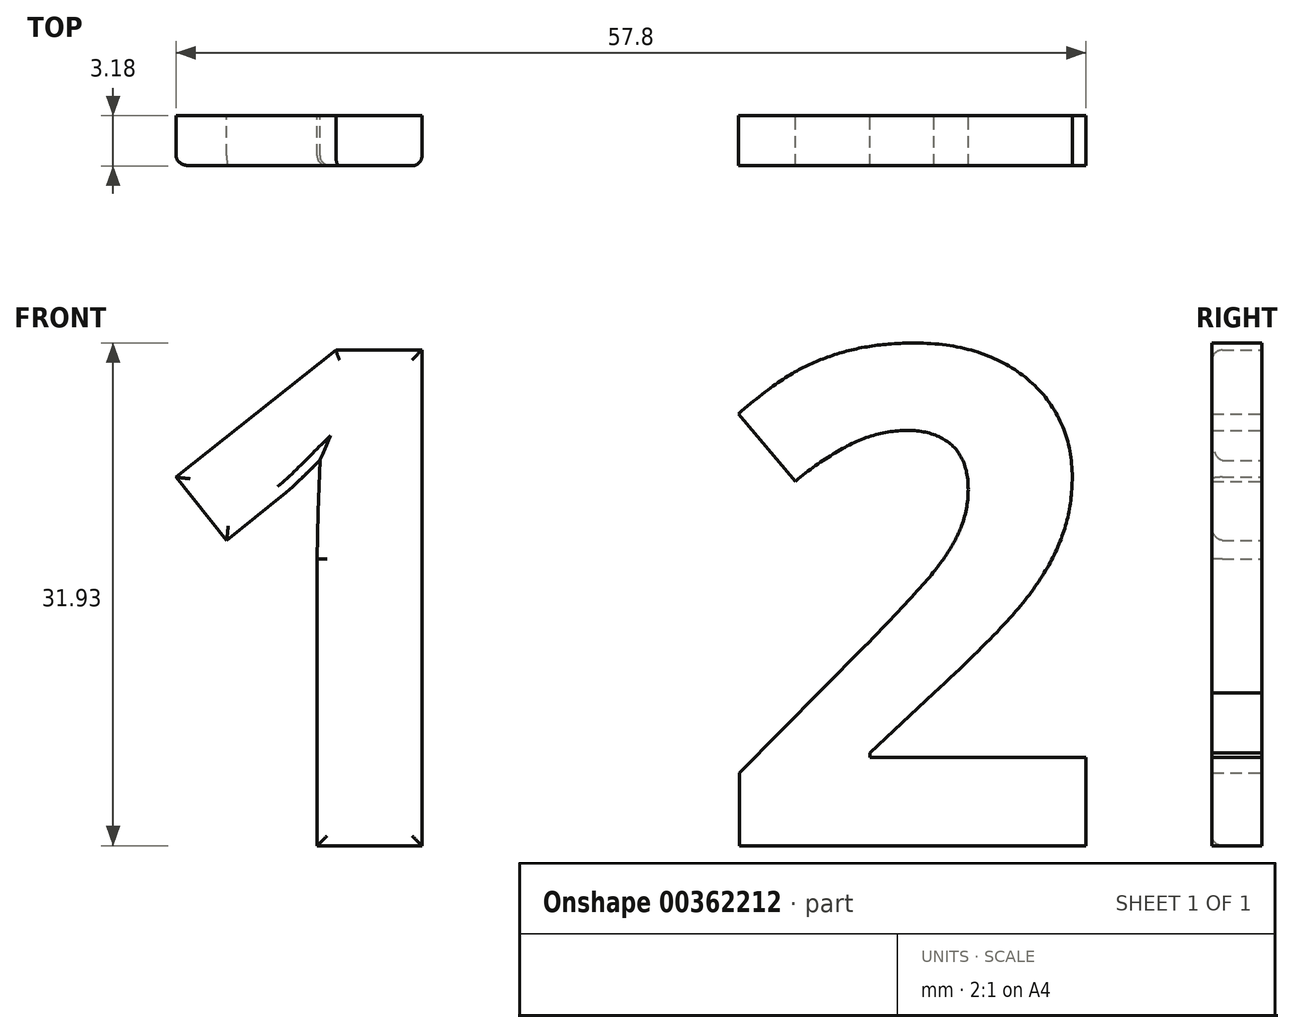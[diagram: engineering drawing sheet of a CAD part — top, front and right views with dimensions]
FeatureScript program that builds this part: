
annotation { "Feature Type Name" : "Feature", "Feature Type Description" : "" }
export const myFeature = defineFeature(function(context is Context, id is Id, definition is map)
    precondition{}
    {
        {
            var Q0;
            Q0=qCreatedBy(makeId("Front.planeOp"),FACE);
            var sketch = newSketch(context, id + "F0", { "sketchPlane" : qUnion([Q0])});
            skText(sketch, "E0", { "text": "1 2", "fontName": "OpenSans-Bold.ttf"});
            const initialGuessF0  = {"E0": [0, -0.03175, 1, 0, 0.03175]};
            skSetInitialGuess(sketch, initialGuessF0);
            skSolve(sketch);
        }
        {
            var Q0;
            Q0 = qSketchRegion(id + "F0", true);
            extrude(context, id + "F1", {"entities" : qUnion([Q0]), "depth" : 3.17 * mm});
        }
        {
            var Q0;
            Q0=makeQuery(id+"F1.opExtrude","CAP_EDGE",EDGE,{"disambiguationData":[OSD([sQuery(id+"F0.wireOp",EDGE,"E0.sketch_text.stroke-8")])],"isStart":false});
            var Q1;
            Q1=makeQuery(id+"F1.opExtrude","CAP_EDGE",EDGE,{"disambiguationData":[OSD([sQuery(id+"F0.wireOp",EDGE,"E0.sketch_text.stroke-7")])],"isStart":false});
            var Q2;
            Q2=makeQuery(id+"F1.opExtrude","CAP_EDGE",EDGE,{"disambiguationData":[OSD([sQuery(id+"F0.wireOp",EDGE,"E0.sketch_text.stroke-6")])],"isStart":false});
            var Q3;
            Q3=makeQuery(id+"F1.opExtrude","CAP_EDGE",EDGE,{"disambiguationData":[OSD([sQuery(id+"F0.wireOp",EDGE,"E0.sketch_text.stroke-5")])],"isStart":false});
            var Q4;
            Q4=makeQuery(id+"F1.opExtrude","CAP_EDGE",EDGE,{"disambiguationData":[OSD([sQuery(id+"F0.wireOp",EDGE,"E0.sketch_text.stroke-4")])],"isStart":false});
            var Q5;
            Q5=makeQuery(id+"F1.opExtrude","CAP_EDGE",EDGE,{"disambiguationData":[OSD([sQuery(id+"F0.wireOp",EDGE,"E0.sketch_text.stroke-1")])],"isStart":false});
            var Q6;
            Q6=makeQuery(id+"F1.opExtrude","CAP_EDGE",EDGE,{"disambiguationData":[OSD([sQuery(id+"F0.wireOp",EDGE,"E0.sketch_text.stroke-2")])],"isStart":false});
            var Q7;
            Q7=makeQuery(id+"F1.opExtrude","CAP_EDGE",EDGE,{"disambiguationData":[OSD([sQuery(id+"F0.wireOp",EDGE,"E0.sketch_text.stroke-3")])],"isStart":false});
            var Q8;
            Q8=makeQuery(id+"F1.opExtrude","CAP_EDGE",EDGE,{"disambiguationData":[OSD([sQuery(id+"F0.wireOp",EDGE,"E0.sketch_text.stroke-0")])],"isStart":false});
            var Q9;
            Q9=makeQuery(id+"F1.opExtrude","CAP_EDGE",EDGE,{"disambiguationData":[OSD([sQuery(id+"F0.wireOp",EDGE,"E0.sketch_text.stroke-9")])],"isStart":false});
            fillet(context, id + "F2", {"entities" : qUnion([Q0, Q1, Q2, Q3, Q4, Q5, Q6, Q7, Q8, Q9]), "radius" : 0.64 * mm, "tangentPropagation" : true, "allowEdgeOverflow" : false});
        }
    });
